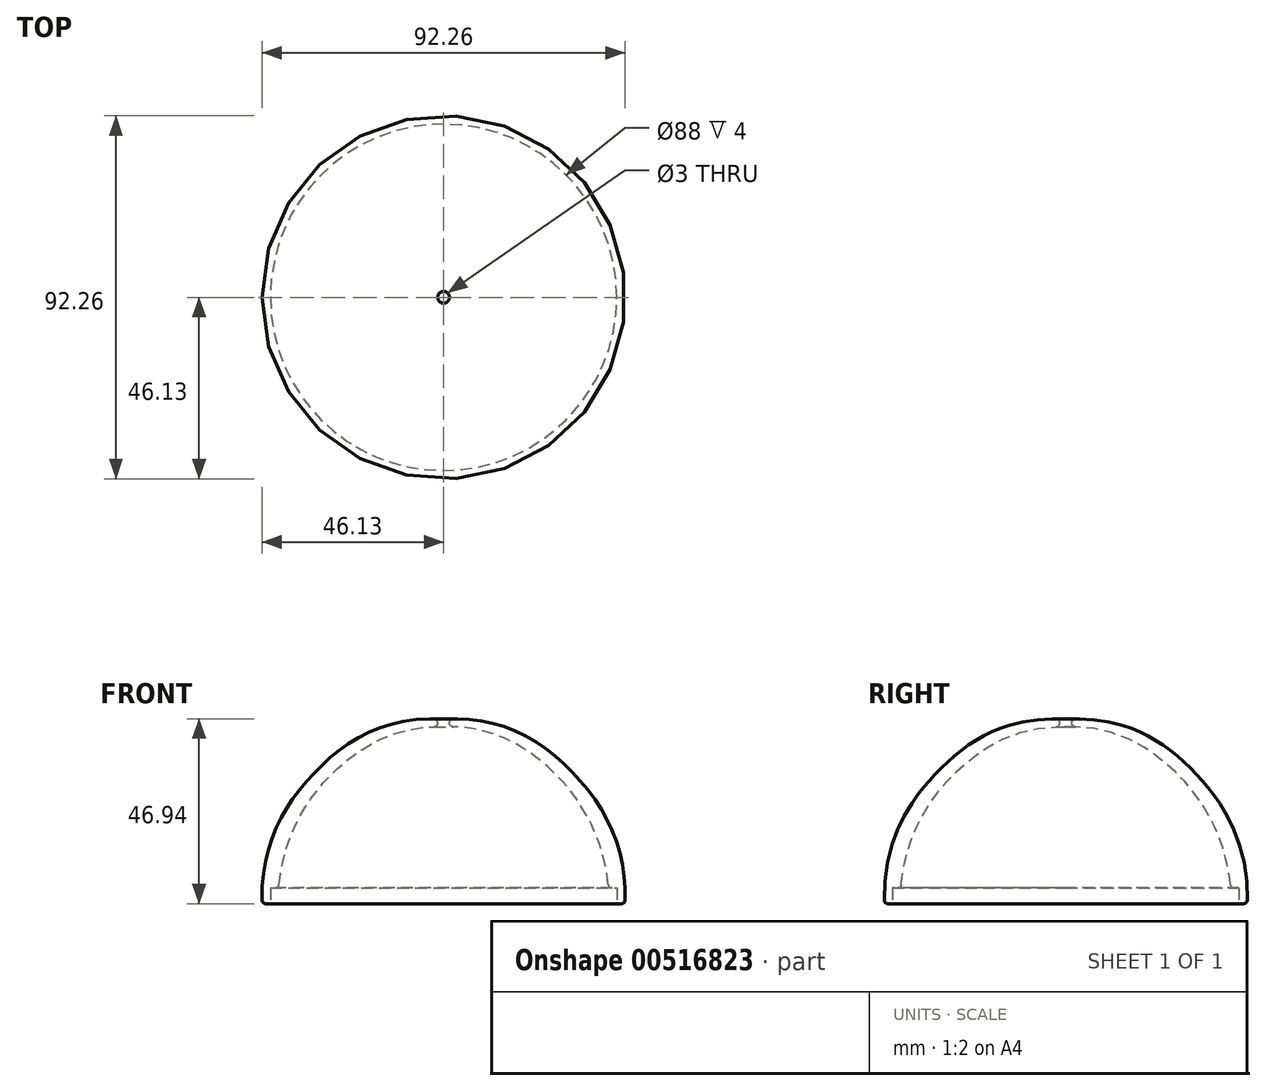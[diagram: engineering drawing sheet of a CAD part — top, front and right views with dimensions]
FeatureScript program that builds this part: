
annotation { "Feature Type Name" : "Feature", "Feature Type Description" : "" }
export const myFeature = defineFeature(function(context is Context, id is Id, definition is map)
    precondition{}
    {
        {
            var Q0;
            Q0=qCreatedBy(makeId("Front.planeOp"),FACE);
            var sketch = newSketch(context, id + "F0", { "sketchPlane" : qUnion([Q0])});
            skLineSegment(sketch, "E0", {"start": v(0, 0) * mm, "end": v(0, 45) * mm, "construction": true});
            skLineSegment(sketch, "E1", {"start": v(0, 0) * mm, "end": v(0, -45) * mm, "construction": true});
            skLineSegment(sketch, "E2", {"start": v(0, 0) * mm, "end": v(-45, 0) * mm, "construction": true});
            skSolve(sketch);
        }
        {
            var Q0;
            Q0=qCreatedBy(makeId("Front.planeOp"),FACE);
            var sketch = newSketch(context, id + "F1", { "sketchPlane" : qUnion([Q0])});
            skLineSegment(sketch, "E3", {"start": v(-46.1, 0) * mm, "end": v(-44, 0) * mm});
            skLineSegment(sketch, "E4", {"start": v(-44, 0) * mm, "end": v(-44, 4) * mm});
            skLineSegment(sketch, "E5", {"start": v(-44, 4) * mm, "end": v(-41.9, 4) * mm});
            skLineSegment(sketch, "E6", {"start": v(0, 44.94) * mm, "end": v(-1.5, 44.94) * mm, "construction": true});
            skFitSpline(sketch, "E7", {"points": [v(-41.9, 4) * mm, v(-29.99, 31.28) * mm, v(-1.5, 44.94) * mm], "startDerivative": vector(6.04, 66.31) * mm, "endDerivative": vector(69.52, -0.8) * mm});
            skLineSegment(sketch, "E8", {"start": v(-1.5, 44.94) * mm, "end": v(-1.5, 46.94) * mm});
            skLineSegment(sketch, "E9", {"start": v(-1.5, 46.94) * mm, "end": v(-3.5, 46.94) * mm});
            skFitSpline(sketch, "E10", {"points": [v(-3.5, 46.94) * mm, v(-34.22, 31.77) * mm, v(-46.1, 0) * mm], "startDerivative": vector(-82.6, -0.7) * mm, "endDerivative": vector(2.7, -83.57) * mm});
            skSolve(sketch);
        }
        {
            var Q0;
            Q0=qSketchRegion(id+"F1",true);
            var Q1;
            Q1=sQuery(id+"F0.wireOp",EDGE,"E0");
            revolve(context, id + "F2", {"entities" : qUnion([Q0]), "axis" : qUnion([Q1]), "revolveType" : RevolveType.FULL});
        }
        {
            var Q0;
            Q0=makeQuery(id+"F2.opRevolve","SWEPT_EDGE",EDGE,{"disambiguationData":[OSD([sQuery(id+"F1.wireOp",EDGE,"E8"),sQuery(id+"F1.wireOp",EDGE,"E9")])]});
            var Q1;
            Q1=makeQuery(id+"F2.opRevolve","SWEPT_EDGE",EDGE,{"disambiguationData":[OSD([sQuery(id+"F1.wireOp",EDGE,"E7"),sQuery(id+"F1.wireOp",EDGE,"E8")])]});
            var Q2;
            Q2=makeQuery(id+"F2.opRevolve","SWEPT_EDGE",EDGE,{"disambiguationData":[OSD([sQuery(id+"F1.wireOp",EDGE,"E5"),sQuery(id+"F1.wireOp",EDGE,"E7")])]});
            fillet(context, id + "F3", {"entities" : qUnion([Q0, Q1, Q2]), "radius" : 1 * mm, "tangentPropagation" : true, "allowEdgeOverflow" : false});
        }
        {
            var Q0;
            Q0=makeQuery(id+"F2.opRevolve","SWEPT_EDGE",EDGE,{"disambiguationData":[OSD([sQuery(id+"F1.wireOp",EDGE,"E3"),sQuery(id+"F1.wireOp",EDGE,"E10")])]});
            fillet(context, id + "F4", {"entities" : qUnion([Q0]), "radius" : 1 * mm, "tangentPropagation" : true, "allowEdgeOverflow" : false});
        }
    });
